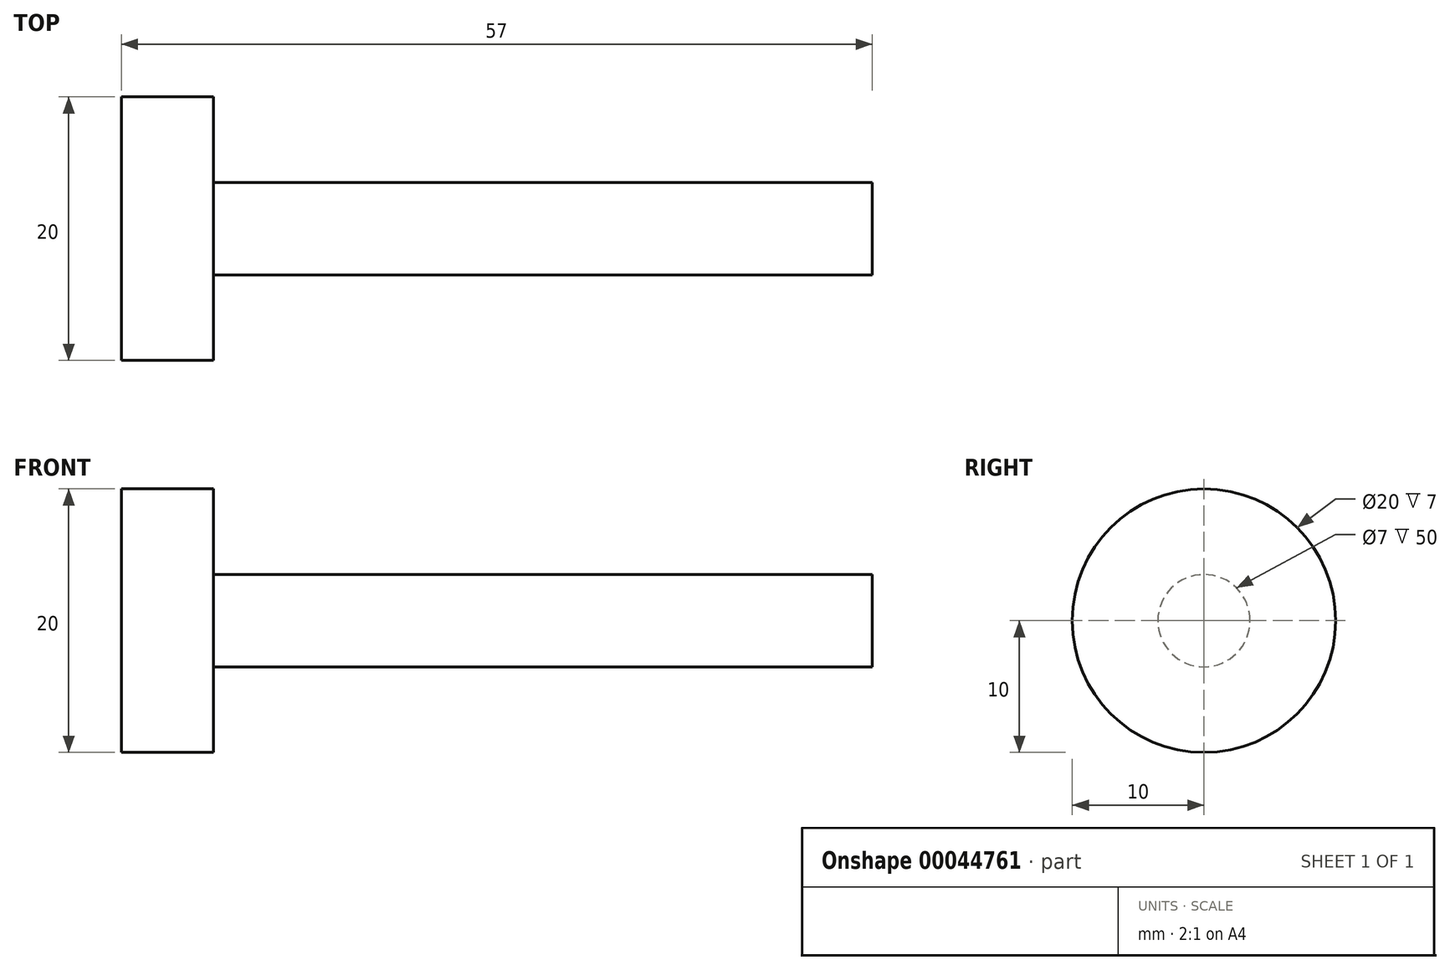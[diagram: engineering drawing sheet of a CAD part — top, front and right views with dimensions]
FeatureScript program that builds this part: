
annotation { "Feature Type Name" : "Feature", "Feature Type Description" : "" }
export const myFeature = defineFeature(function(context is Context, id is Id, definition is map)
    precondition{}
    {
        {
            var Q0;
            Q0=qCreatedBy(makeId("Top.planeOp"),FACE);
            var sketch = newSketch(context, id + "F0", { "sketchPlane" : qUnion([Q0])});
            skLineSegment(sketch, "E0.bottom", {"start": v(-27.79, -3.5) * mm, "end": v(22.21, -3.5) * mm});
            skLineSegment(sketch, "E0.top", {"start": v(-27.79, 3.5) * mm, "end": v(22.21, 3.5) * mm});
            skLineSegment(sketch, "E0.left", {"start": v(-27.79, -3.5) * mm, "end": v(-27.79, 3.5) * mm});
            skLineSegment(sketch, "E0.right", {"start": v(22.21, -3.5) * mm, "end": v(22.21, 0) * mm});
            skLineSegment(sketch, "E1.bottom", {"start": v(-27.79, -10) * mm, "end": v(-34.79, -10) * mm});
            skLineSegment(sketch, "E1.top", {"start": v(-27.79, 10) * mm, "end": v(-34.79, 10) * mm});
            skLineSegment(sketch, "E1.left", {"start": v(-27.79, -10) * mm, "end": v(-27.79, -3.5) * mm});
            skLineSegment(sketch, "E1.right", {"start": v(-34.79, -10) * mm, "end": v(-34.79, 0) * mm});
            skLineSegment(sketch, "E2", {"start": v(-30.56, 0) * mm, "end": v(27.43, 0) * mm, "construction": true});
            skLineSegment(sketch, "E3", {"start": v(22.21, 0) * mm, "end": v(22.21, 3.5) * mm});
            skLineSegment(sketch, "E4", {"start": v(-34.79, 0) * mm, "end": v(-34.79, 10) * mm});
            skLineSegment(sketch, "E5", {"start": v(-27.79, 0) * mm, "end": v(-27.79, 10) * mm});
            skLineSegment(sketch, "E6", {"start": v(-27.79, -3.5) * mm, "end": v(-27.79, 0) * mm});
            skSolve(sketch);
        }
        {
            var Q0;
            Q0=sQuery(id+"F0.wireOp",EDGE,"E0.bottom");
            var Q1;
            Q1=sQuery(id+"F0.wireOp",EDGE,"E1.left");
            var Q2;
            Q2=sQuery(id+"F0.wireOp",EDGE,"E1.bottom");
            var Q3;
            Q3=sQuery(id+"F0.wireOp",EDGE,"E1.right");
            var Q4;
            Q4=sQuery(id+"F0.wireOp",EDGE,"E0.right");
            var Q5;
            Q5=sQuery(id+"F0.wireOp",EDGE,"E2");
            revolve(context, id + "F1", {"bodyType" : ToolBodyType.SURFACE, "operationType" : NewBodyOperationType.ADD, "surfaceOperationType" : NewSurfaceOperationType.NEW, "surfaceEntities" : qUnion([Q0, Q1, Q2, Q3, Q4]), "axis" : qUnion([Q5]), "revolveType" : RevolveType.FULL});
        }
    });
